# Revit family: Faucet-Two_Handle-American_Standard-Monterrey-750X.145-175_Series
name_source: partatom
category: Plumbing Fixtures
units: mm (PartAtom-declared; Revit-internal decimal feet)

## family parameters
Always vertical = No
Cut with Voids When Loaded = No
OmniClass Number = 23.45.55.14
OmniClass Title = Single Faucets
Part Type = Normal
Room Calculation Point = No
Round Connector Dimension = Use Diameter
Shared = Yes
Work Plane-Based = No

## types (2) — shared parameters
ADA Compliant = Yes
Assembly Code = D2020300
CEC Compliant = Yes
CW Connection = Yes
CWFU = 1.5
CalGreen Compliant = Yes
Cold Water Connection Diameter = 1/2"
Compliance Certifications = These products meet or exceeds: ANSI A117.1, ASME A112.18.1, CSA B 125, NSF 372
Extrusion Start = -5/8"
Finish = Brass-American Standard-002-Polished Chrome
Flow Rate = 0.5 gpm/1.9 Lpm
HW Connection = Yes
HWFU = 1.5
Height = 10 3/4"
Hot Water Connection Diameter = 1/2"
Installation Type = Wall Mounted
Length = 4"
Manufacturer = American Standard
Material = Brass-American Standard-002-Polished Chrome
Pop-Up Hole & Rod = Yes
Price = Prices may vary. Please consult Manufacturer Representative for most up-to-date price list.
Product Documentation Link = https://americanstandard.box.com
Product Page URL = https://www.americanstandard-us.com
Revised Date = 02/21/2023
URL = http://www.americanstandard-us.com
Vent Connection = No
Void End 2 = 1/2"
WFU = 2
Warranty Information = Faucet Lifetime Function and Finish Limited Warranty
Waste Connection = No
Width = 1 13/16"

## per-type parameters (varying)
| type | Description | Extrusion End | Handle Length | Void Start 2 |
| 7500175.002 | Monterrey® 4-Inch Centerset Gooseneck Faucet With Wrist Blade Handles 0.5 gpm/1.9 Lpm | -1/2" | 3 7/8" | -11/32" |
| 7500145.002 | Monterrey® 4-Inch Centerset Gooseneck Faucet With Lever Handles 0.5 gpm/1.9 Lpm | 11/32" | 2 1/4" | 13/32" |

note: column(s) folded — value = type name in every type: Model

## geometry (parser evidence)
native form markers: Extrusion x2, Sweep x2
no freeform markers — native parametric forms only
